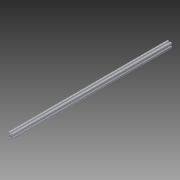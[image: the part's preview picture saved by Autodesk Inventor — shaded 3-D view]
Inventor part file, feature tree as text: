
AUTODESK INVENTOR PART (.ipt)
format: ipt  version: 2013 (Build 170138000, 138)  size: 287,232 bytes
history: native  units: in
note: dims shown in document units (in); Inventor stores cm internally (conversion verified against a paired STEP export)
features: extrude x1, sketch x1
ambient origin geometry x8: Origin, YZ Plane, XZ Plane, XY Plane, X Axis, Y Axis, Z Axis, Center Point
bodies: Solid1 (feature_tree)
feature tree (2):
  extrude  "Extrusion1"  [1 undecoded]
  sketch  "Sketch1"  dims[d0=49.0in d1=0.0in]
note: 1 required parameter value undecoded (feature->parameter linkage not recoverable at this tier; creation-order binding heuristic only, values carry confidence <= 0.55)
